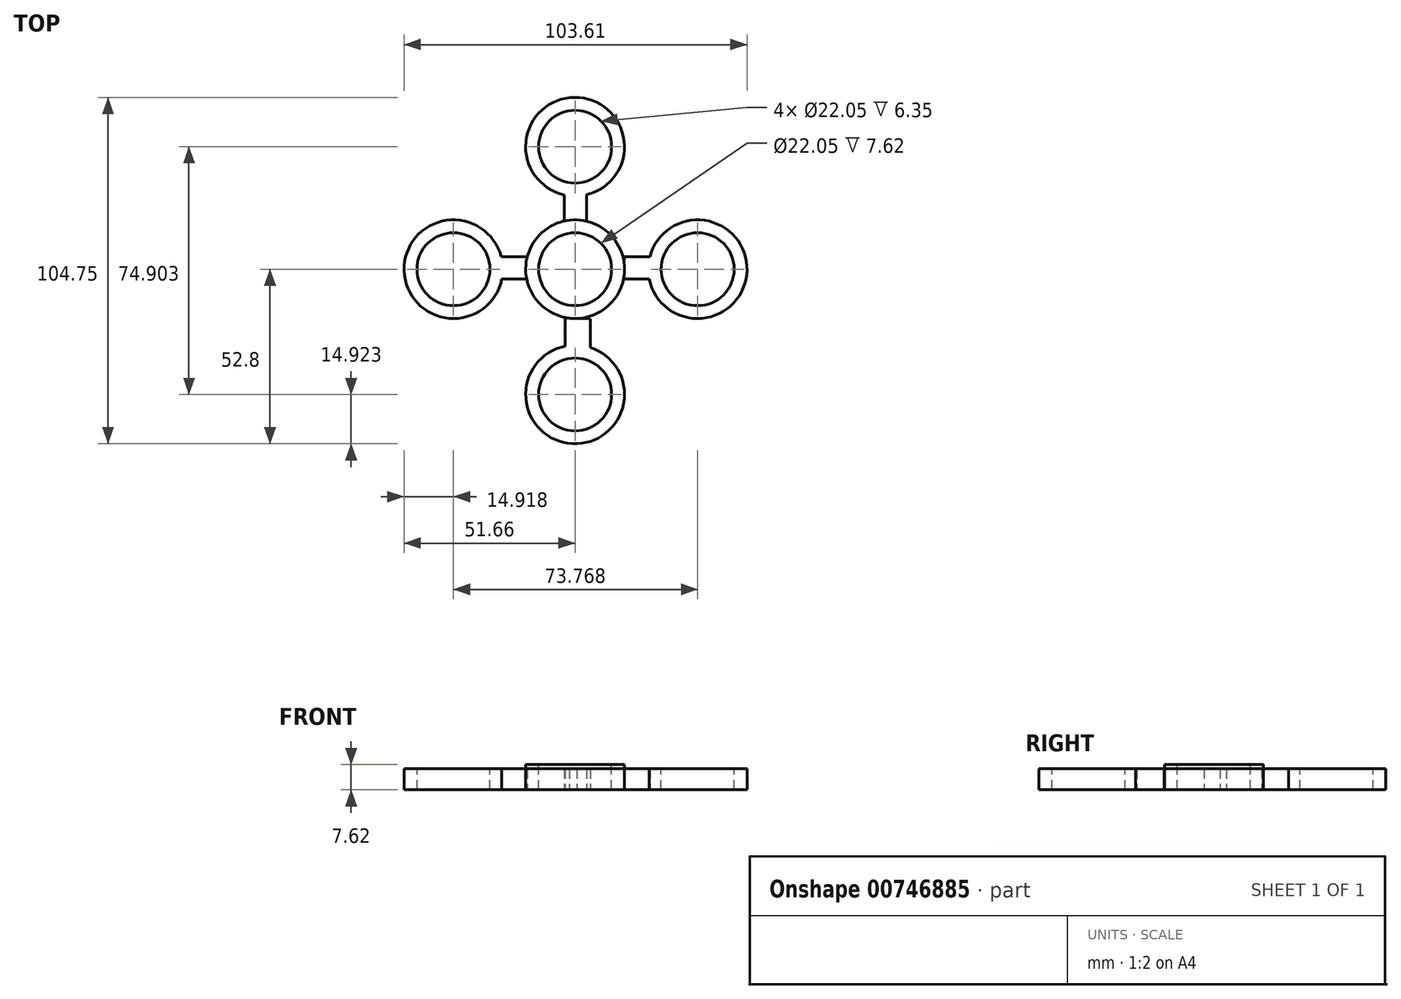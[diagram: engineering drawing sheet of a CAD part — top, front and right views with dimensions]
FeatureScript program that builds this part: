
annotation { "Feature Type Name" : "Feature", "Feature Type Description" : "" }
export const myFeature = defineFeature(function(context is Context, id is Id, definition is map)
    precondition{}
    {
        {
            var Q0;
            Q0=qCreatedBy(makeId("Top.planeOp"),FACE);
            var sketch = newSketch(context, id + "F0", { "sketchPlane" : qUnion([Q0])});
            skCircle(sketch, "E0", {"center": v(0, 0) * mm, "radius": 14.92 * mm});
            skSolve(sketch);
        }
        {
            var Q0;
            Q0 = qSketchRegion(id + "F0", true);
            extrude(context, id + "F1", {"entities" : qUnion([Q0]), "depth" : 7.62 * mm, "offsetDistance" : 25.4 * mm});
        }
        {
            var Q0;
            Q0=makeQuery(id+"F1.opExtrude","CAP_FACE",FACE,{"disambiguationData":[OSD([sQuery(id+"F0.wireOp",EDGE,"E0")])],"isStart":false});
            var sketch = newSketch(context, id + "F2", { "sketchPlane" : qUnion([Q0])});
            skCircle(sketch, "E1", {"center": v(0, 0) * mm, "radius": 11.02 * mm});
            skSolve(sketch);
        }
        {
            var Q0;
            Q0 = qSketchRegion(id + "F2", true);
            extrude(context, id + "F3", {"entities" : qUnion([Q0]), "operationType" : NewBodyOperationType.REMOVE, "oppositeDirection" : true, "depth" : 25.4 * mm, "offsetDistance" : 25.4 * mm});
        }
        {
            var Q0;
            Q0=qCreatedBy(makeId("Top.planeOp"),FACE);
            var sketch = newSketch(context, id + "F4", { "sketchPlane" : qUnion([Q0])});
            skLineSegment(sketch, "E2", {"start": v(14.9, 3.83) * mm, "end": v(23.4, 3.83) * mm});
            skLineSegment(sketch, "E3", {"start": v(23.4, 3.83) * mm, "end": v(23.4, -2.98) * mm});
            skLineSegment(sketch, "E4", {"start": v(23.4, -2.98) * mm, "end": v(14.61, -2.98) * mm});
            skLineSegment(sketch, "E5", {"start": v(14.61, -2.98) * mm, "end": v(14.9, 3.83) * mm});
            skLineSegment(sketch, "E6", {"start": v(-3.28, 14.61) * mm, "end": v(-3.28, 23.12) * mm});
            skLineSegment(sketch, "E7", {"start": v(-3.28, 23.12) * mm, "end": v(3.53, 23.12) * mm});
            skLineSegment(sketch, "E8", {"start": v(3.53, 23.12) * mm, "end": v(3.53, 14.33) * mm});
            skLineSegment(sketch, "E9", {"start": v(3.53, 14.33) * mm, "end": v(-3.28, 14.61) * mm});
            skLineSegment(sketch, "E10", {"start": v(-22.74, 3.83) * mm, "end": v(-14.23, 3.83) * mm});
            skLineSegment(sketch, "E11", {"start": v(-14.23, 3.83) * mm, "end": v(-14.23, -2.98) * mm});
            skLineSegment(sketch, "E12", {"start": v(-14.23, -2.98) * mm, "end": v(-23.03, -2.98) * mm});
            skLineSegment(sketch, "E13", {"start": v(-23.03, -2.98) * mm, "end": v(-22.74, 3.83) * mm});
            skLineSegment(sketch, "E14", {"start": v(4.6, -15.06) * mm, "end": v(4.6, -23.89) * mm});
            skLineSegment(sketch, "E15", {"start": v(4.6, -23.89) * mm, "end": v(-3.06, -23.89) * mm});
            skLineSegment(sketch, "E16", {"start": v(-3.06, -23.89) * mm, "end": v(-3.06, -14.77) * mm});
            skLineSegment(sketch, "E17", {"start": v(-3.06, -14.77) * mm, "end": v(4.6, -15.06) * mm});
            skSolve(sketch);
        }
        {
            var Q0;
            Q0 = qSketchRegion(id + "F4", true);
            extrude(context, id + "F5", {"entities" : qUnion([Q0]), "operationType" : NewBodyOperationType.ADD, "depth" : 6.35 * mm, "offsetDistance" : 25.4 * mm});
        }
        {
            var Q0;
            Q0=qCreatedBy(makeId("Top.planeOp"),FACE);
            var sketch = newSketch(context, id + "F6", { "sketchPlane" : qUnion([Q0])});
            skCircle(sketch, "E18", {"center": v(37.03, 0) * mm, "radius": 14.92 * mm});
            skCircle(sketch, "E19", {"center": v(0, 37.03) * mm, "radius": 14.92 * mm});
            skCircle(sketch, "E20", {"center": v(-36.74, 0) * mm, "radius": 14.92 * mm});
            skCircle(sketch, "E21", {"center": v(0, -37.88) * mm, "radius": 14.92 * mm});
            skSolve(sketch);
        }
        {
            var Q0;
            Q0 = qSketchRegion(id + "F6", true);
            extrude(context, id + "F7", {"entities" : qUnion([Q0]), "operationType" : NewBodyOperationType.ADD, "depth" : 6.35 * mm, "offsetDistance" : 25.4 * mm});
        }
        {
            var Q0;
            Q0=makeQuery(id+"F7.opExtrude","CAP_FACE",FACE,{"disambiguationData":[OSD([sQuery(id+"F6.wireOp",EDGE,"E20")])],"isStart":false});
            var sketch = newSketch(context, id + "F8", { "sketchPlane" : qUnion([Q0])});
            skCircle(sketch, "E22", {"center": v(-36.74, 0) * mm, "radius": 11.02 * mm});
            skSolve(sketch);
        }
        {
            var Q0;
            Q0 = qSketchRegion(id + "F8", true);
            extrude(context, id + "F9", {"entities" : qUnion([Q0]), "operationType" : NewBodyOperationType.REMOVE, "oppositeDirection" : true, "depth" : 25.4 * mm, "offsetDistance" : 25.4 * mm});
        }
        {
            var Q0;
            Q0=makeQuery(id+"F7.opExtrude","CAP_FACE",FACE,{"disambiguationData":[OSD([sQuery(id+"F6.wireOp",EDGE,"E19")])],"isStart":false});
            var sketch = newSketch(context, id + "F10", { "sketchPlane" : qUnion([Q0])});
            skCircle(sketch, "E23", {"center": v(0, 37.03) * mm, "radius": 11.02 * mm});
            skSolve(sketch);
        }
        {
            var Q0;
            Q0 = qSketchRegion(id + "F10", true);
            extrude(context, id + "F11", {"entities" : qUnion([Q0]), "operationType" : NewBodyOperationType.REMOVE, "oppositeDirection" : true, "depth" : 25.4 * mm, "offsetDistance" : 25.4 * mm});
        }
        {
            var Q0;
            Q0=makeQuery(id+"F7.opExtrude","CAP_FACE",FACE,{"disambiguationData":[OSD([sQuery(id+"F6.wireOp",EDGE,"E18")])],"isStart":false});
            var sketch = newSketch(context, id + "F12", { "sketchPlane" : qUnion([Q0])});
            skCircle(sketch, "E24", {"center": v(37.03, 0) * mm, "radius": 11.02 * mm});
            skSolve(sketch);
        }
        {
            var Q0;
            Q0 = qSketchRegion(id + "F12", true);
            extrude(context, id + "F13", {"entities" : qUnion([Q0]), "operationType" : NewBodyOperationType.REMOVE, "oppositeDirection" : true, "depth" : 25.4 * mm, "offsetDistance" : 25.4 * mm});
        }
        {
            var Q0;
            Q0=makeQuery(id+"F7.opExtrude","CAP_FACE",FACE,{"disambiguationData":[OSD([sQuery(id+"F6.wireOp",EDGE,"E21")])],"isStart":false});
            var sketch = newSketch(context, id + "F14", { "sketchPlane" : qUnion([Q0])});
            skCircle(sketch, "E25", {"center": v(0, -37.88) * mm, "radius": 11.02 * mm});
            skSolve(sketch);
        }
        {
            var Q0;
            Q0 = qSketchRegion(id + "F14", true);
            extrude(context, id + "F15", {"entities" : qUnion([Q0]), "operationType" : NewBodyOperationType.REMOVE, "oppositeDirection" : true, "depth" : 25.4 * mm, "offsetDistance" : 25.4 * mm});
        }
    });
